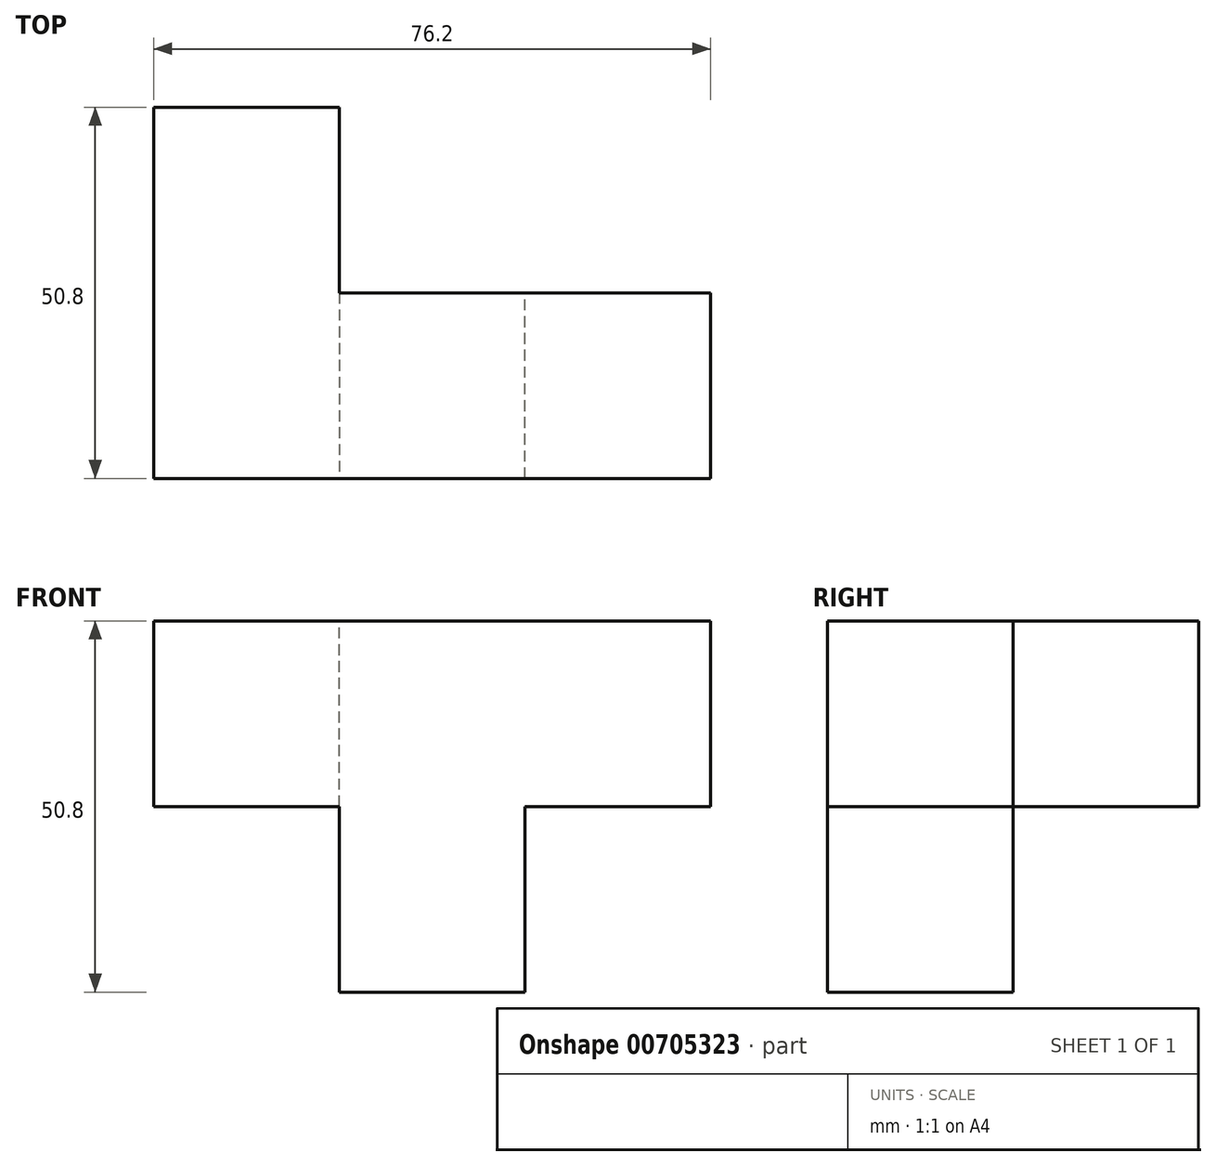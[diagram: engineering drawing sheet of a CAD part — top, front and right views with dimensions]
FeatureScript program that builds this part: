
annotation { "Feature Type Name" : "Feature", "Feature Type Description" : "" }
export const myFeature = defineFeature(function(context is Context, id is Id, definition is map)
    precondition{}
    {
        {
            var Q0;
            Q0=qCreatedBy(makeId("Front.planeOp"),FACE);
            var sketch = newSketch(context, id + "F0", { "sketchPlane" : qUnion([Q0])});
            skLineSegment(sketch, "E0.bottom", {"start": v(-12.73, 0) * mm, "end": v(12.67, 0) * mm});
            skLineSegment(sketch, "E0.top", {"start": v(-12.73, -25.4) * mm, "end": v(12.67, -25.4) * mm});
            skLineSegment(sketch, "E0.left", {"start": v(-12.73, 0) * mm, "end": v(-12.73, -25.4) * mm});
            skLineSegment(sketch, "E0.right", {"start": v(12.67, 0) * mm, "end": v(12.67, -25.4) * mm});
            skLineSegment(sketch, "E1.top", {"start": v(-12.73, 25.4) * mm, "end": v(12.67, 25.4) * mm});
            skLineSegment(sketch, "E1.left", {"start": v(-12.73, 0) * mm, "end": v(-12.73, 25.4) * mm});
            skLineSegment(sketch, "E1.right", {"start": v(12.67, 0) * mm, "end": v(12.67, 25.4) * mm});
            skLineSegment(sketch, "E2.bottom", {"start": v(12.67, 25.4) * mm, "end": v(38.07, 25.4) * mm});
            skLineSegment(sketch, "E2.top", {"start": v(12.67, 0) * mm, "end": v(38.07, 0) * mm});
            skLineSegment(sketch, "E2.left", {"start": v(12.67, 25.4) * mm, "end": v(12.67, 0) * mm});
            skLineSegment(sketch, "E2.right", {"start": v(38.07, 25.4) * mm, "end": v(38.07, 0) * mm});
            skLineSegment(sketch, "E3.bottom", {"start": v(-12.73, 25.4) * mm, "end": v(-38.13, 25.4) * mm});
            skLineSegment(sketch, "E3.top", {"start": v(-12.73, 0) * mm, "end": v(-38.13, 0) * mm});
            skLineSegment(sketch, "E3.left", {"start": v(-12.73, 25.4) * mm, "end": v(-12.73, 0) * mm});
            skLineSegment(sketch, "E3.right", {"start": v(-38.13, 25.4) * mm, "end": v(-38.13, 0) * mm});
            skSolve(sketch);
        }
        {
            var Q0;
            Q0=makeQuery(id+"F0.imprint","IMPRINT",FACE,{"disambiguationData":[TD([[makeQuery(id+"F0.imprint","IMPRINT",EDGE,{"derivedFrom":sQuery(id+"F0.wireOp",EDGE,"E0.bottom")}),1.0]])]});
            var Q1;
            Q1=makeQuery(id+"F0.imprint","IMPRINT",FACE,{"disambiguationData":[TD([[makeQuery(id+"F0.imprint","IMPRINT",EDGE,{"derivedFrom":sQuery(id+"F0.wireOp",EDGE,"E2.bottom")}),-1.0]])]});
            var Q2;
            Q2=makeQuery(id+"F0.imprint","IMPRINT",FACE,{"disambiguationData":[TD([[makeQuery(id+"F0.imprint","IMPRINT",EDGE,{"derivedFrom":sQuery(id+"F0.wireOp",EDGE,"E0.top")}),1.0]])]});
            extrude(context, id + "F1", {"entities" : qUnion([Q0, Q1, Q2]), "depth" : 25.4 * mm, "offsetDistance" : 25.4 * mm});
        }
        {
            var Q0;
            Q0=makeQuery(id+"F0.imprint","IMPRINT",FACE,{"disambiguationData":[TD([[makeQuery(id+"F0.imprint","IMPRINT",EDGE,{"derivedFrom":sQuery(id+"F0.wireOp",EDGE,"E3.bottom")}),1.0]])]});
            extrude(context, id + "F2", {"entities" : qUnion([Q0]), "operationType" : NewBodyOperationType.ADD, "endBound" : BoundingType.SYMMETRIC, "oppositeDirection" : true, "depth" : 50.8 * mm, "offsetDistance" : 25.4 * mm});
        }
    });
